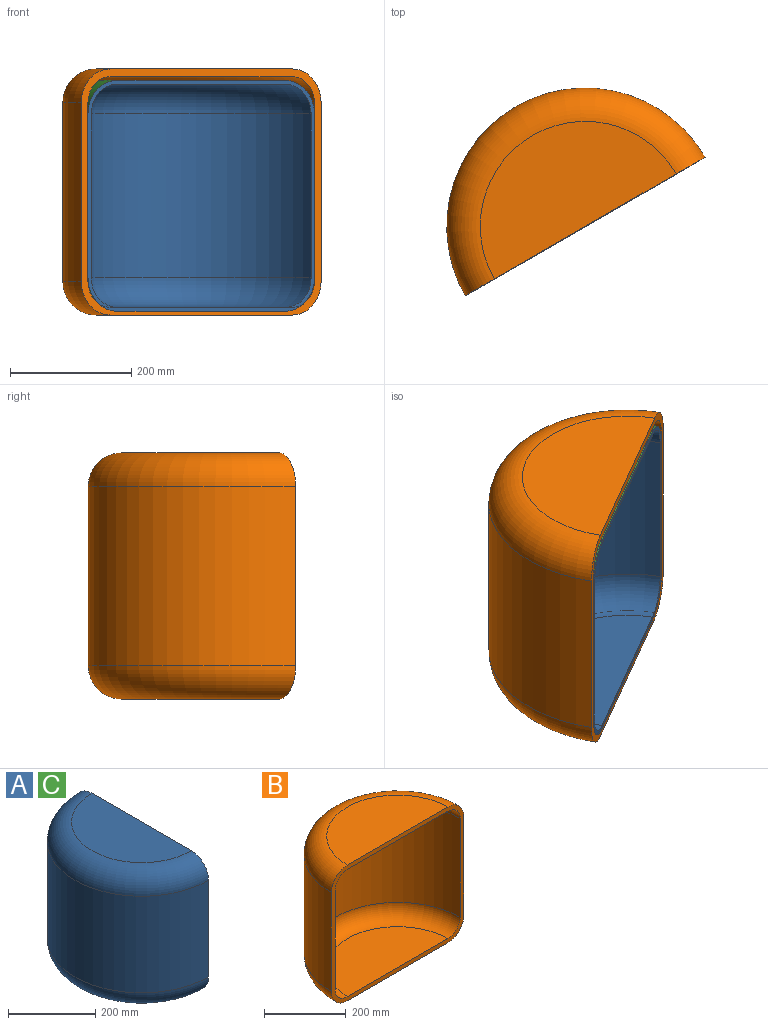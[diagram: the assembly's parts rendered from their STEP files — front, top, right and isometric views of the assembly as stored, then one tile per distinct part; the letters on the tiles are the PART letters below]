
ASSEMBLY  parts=3 mates=1
PART A: 11 faces, bbox 233.7x467.4x381 mm
  f0: plane 431.8x381mm, normal (1,0,0), area 9594.2mm2, adj f1,f2,f3,f4,f5,f6,f7,f8
  f1: cylinder r=215.9mm len=431.8mm, axis (0,0,-1), area 183547.7mm2, adj f0,f4,f5
  f2: plane 321.41x160.71mm, normal (0,0,1), area 40567.9mm2, adj f0,f4
  f3: plane 321.41x160.71mm, normal (0,0,-1), area 40567.9mm2, adj f0,f5
  f4: torus R=160.71mm, axis (0,0,1), area 53342.4mm2, adj f0,f1,f2
  f5: torus R=160.71mm, axis (0,0,1), area 53342.4mm2, adj f0,f1,f3
  f6: cylinder r=209.55mm len=419.1mm, axis (0,0,-1), area 178149.2mm2, adj f0,f9,f10
  f7: plane 321.41x160.71mm, normal (0,0,-1), area 40567.9mm2, adj f0,f9
  f8: plane 321.41x160.71mm, normal (0,0,1), area 40567.9mm2, adj f0,f10
  f9: torus R=160.71mm, axis (0,0,1), area 46231mm2, adj f0,f6,f7
  f10: torus R=160.71mm, axis (0,0,1), area 46231mm2, adj f0,f6,f8
PART B: 11 faces, bbox 494.9x247.4x406.4 mm
  f0: cylinder r=228.6mm len=457.2mm, axis (0,0,-1), area 212586.1mm2, adj f1,f4,f5
  f1: plane 457.2x406.4mm, normal (0,-1,0), area 20225.3mm2, adj f0,f2,f3,f4,f5,f6,f7,f8
  f2: plane 346.81x173.41mm, normal (0,0,1), area 47233.2mm2, adj f1,f4
  f3: plane 346.81x173.41mm, normal (0,0,-1), area 47233.2mm2, adj f1,f5
  f4: torus R=173.41mm, axis (0,0,1), area 56801.5mm2, adj f0,f1,f2
  f5: torus R=173.41mm, axis (0,0,1), area 56801.5mm2, adj f0,f1,f3
  f6: cylinder r=215.9mm len=431.8mm, axis (0,0,-1), area 200775.7mm2, adj f1,f9,f10
  f7: plane 346.81x173.41mm, normal (0,0,-1), area 47233.2mm2, adj f1,f9
  f8: plane 346.81x173.41mm, normal (0,0,1), area 47233.2mm2, adj f1,f10
  f9: torus R=173.41mm, axis (0,0,1), area 42036.2mm2, adj f1,f6,f7
  f10: torus R=173.41mm, axis (0,0,1), area 42036.2mm2, adj f1,f6,f8
PART C: same geometry as A
PLACE A rot(axis=(0.87,-0.5,0),180deg) t=(-139.16,171.1,741.94)mm
PLACE B rot(axis=(-0.26,0.97,0),180deg) t=(-139.16,171.1,760.99)mm
PLACE C rot(axis=(0.87,-0.5,0),180deg) t=(-139.16,171.1,741.94)mm
MATE fastened B.f0 <-> C.f1  axis (0,0,-1) through (-139.16,171.1,367.29)mm
